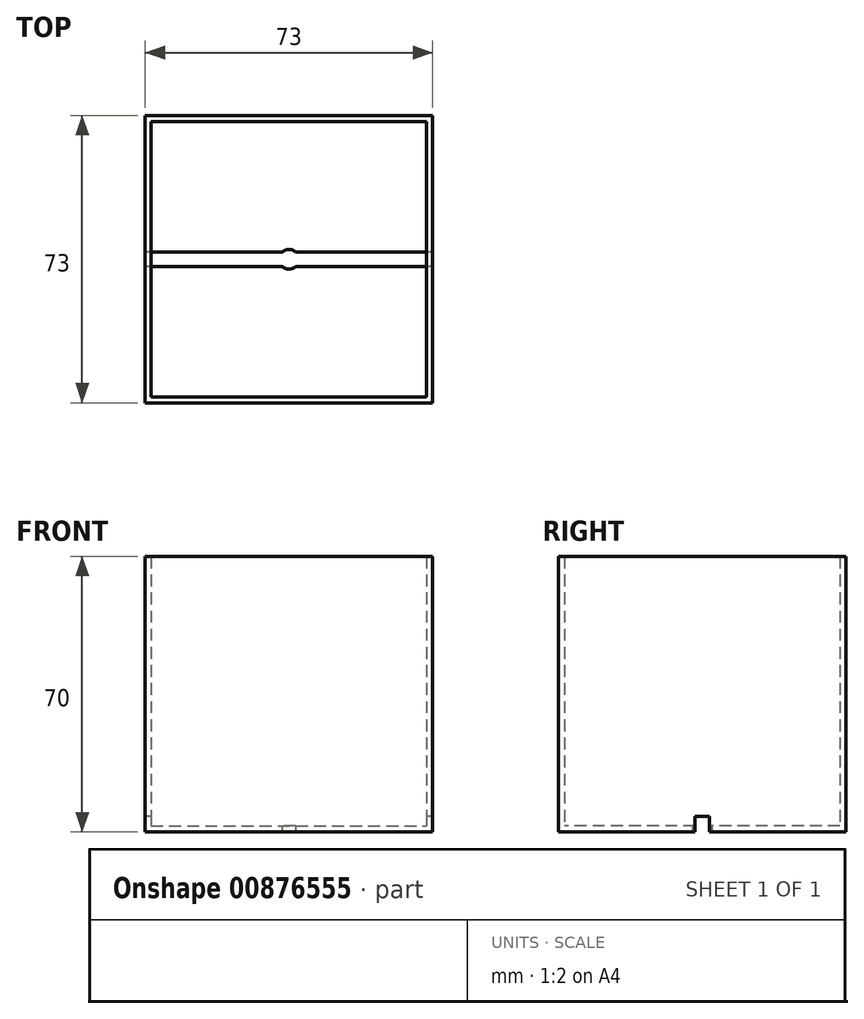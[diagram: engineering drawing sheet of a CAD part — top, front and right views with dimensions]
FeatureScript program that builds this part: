
annotation { "Feature Type Name" : "Feature", "Feature Type Description" : "" }
export const myFeature = defineFeature(function(context is Context, id is Id, definition is map)
    precondition{}
    {
        {
            var Q0;
            Q0=qCreatedBy(makeId("Top.planeOp"),FACE);
            var sketch = newSketch(context, id + "F0", { "sketchPlane" : qUnion([Q0])});
            skLineSegment(sketch, "E0.bottom", {"start": v(-36.5, 36.5) * mm, "end": v(36.5, 36.5) * mm});
            skLineSegment(sketch, "E0.top", {"start": v(-36.5, -36.5) * mm, "end": v(36.5, -36.5) * mm});
            skLineSegment(sketch, "E0.left", {"start": v(-36.5, 36.5) * mm, "end": v(-36.5, -36.5) * mm});
            skLineSegment(sketch, "E0.right", {"start": v(36.5, 36.5) * mm, "end": v(36.5, -36.5) * mm});
            skPoint(sketch, "E0.middle", {"position": v(0, 0) * mm});
            skSolve(sketch);
        }
        {
            var Q0;
            Q0=makeQuery(id+"F0.imprint","IMPRINT",FACE,{"disambiguationData":[TD([[makeQuery(id+"F0.imprint","IMPRINT",EDGE,{"derivedFrom":sQuery(id+"F0.wireOp",EDGE,"E0.bottom")}),-1.0]])]});
            extrude(context, id + "F1", {"entities" : qUnion([Q0]), "depth" : 70 * mm, "offsetDistance" : 25 * mm});
        }
        {
            var Q0;
            Q0=makeQuery(id+"F1.opExtrude","CAP_FACE",FACE,{"disambiguationData":[OSD([sQuery(id+"F0.wireOp",EDGE,"E0.bottom"),sQuery(id+"F0.wireOp",EDGE,"E0.top"),sQuery(id+"F0.wireOp",EDGE,"E0.left"),sQuery(id+"F0.wireOp",EDGE,"E0.right")])],"isStart":false});
            shell(context, id + "F2", {"entities" : qUnion([Q0]), "thickness" : 1.5 * mm});
        }
        {
            var Q0;
            Q0=makeQuery(id+"F1.opExtrude","CAP_FACE",FACE,{"disambiguationData":[OSD([sQuery(id+"F0.wireOp",EDGE,"E0.bottom"),sQuery(id+"F0.wireOp",EDGE,"E0.top"),sQuery(id+"F0.wireOp",EDGE,"E0.left"),sQuery(id+"F0.wireOp",EDGE,"E0.right")])],"isStart":true});
            var sketch = newSketch(context, id + "F3", { "sketchPlane" : qUnion([Q0])});
            skLineSegment(sketch, "E1.bottom", {"start": v(36.5, -1.8) * mm, "end": v(-36.5, -1.8) * mm});
            skLineSegment(sketch, "E1.top", {"start": v(36.5, 1.8) * mm, "end": v(-36.5, 1.8) * mm});
            skLineSegment(sketch, "E1.left", {"start": v(36.5, -1.8) * mm, "end": v(36.5, 1.8) * mm});
            skLineSegment(sketch, "E1.right", {"start": v(-36.5, -1.8) * mm, "end": v(-36.5, 1.8) * mm});
            skCircle(sketch, "E2", {"center": v(0, 0) * mm, "radius": 2.5 * mm});
            skSolve(sketch);
        }
        {
            var Q0;
            Q0 = qSketchRegion(id + "F3", true);
            extrude(context, id + "F4", {"entities" : qUnion([Q0]), "operationType" : NewBodyOperationType.REMOVE, "oppositeDirection" : true, "depth" : 4 * mm, "offsetDistance" : 25 * mm});
        }
    });
